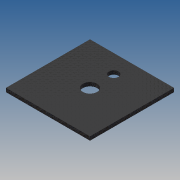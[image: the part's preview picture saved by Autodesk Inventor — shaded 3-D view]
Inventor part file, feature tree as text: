
AUTODESK INVENTOR PART (.ipt)
format: ipt  version: 2014 SP1 (Build 180222100, 222)  size: 93,696 bytes
history: native  units: in
note: dims shown in document units (in); Inventor stores cm internally (conversion verified against a paired STEP export)
features: extrude x3, sketch x3
ambient origin geometry x8: Origin, YZ Plane, XZ Plane, XY Plane, X Axis, Y Axis, Z Axis, Center Point
bodies: Solid1 (feature_tree)
feature tree (6):
  extrude  "Extrusion1"  Depth=35.4331in
  extrude  "Extrusion2"  Depth=1.5748in
  extrude  "Extrusion3"  Depth=4.0in
  sketch  "Sketch1"  dims[d0=35.4331in d1=35.4331in]
  sketch  "Sketch2"  dims[d2=1.5748in d3=0.0in d4=6.0in]
  sketch  "Sketch3"  dims[d5=1.0in d6=0.0in d7=4.0in d8=10.0in d9=10.0in d10=0.0in]
